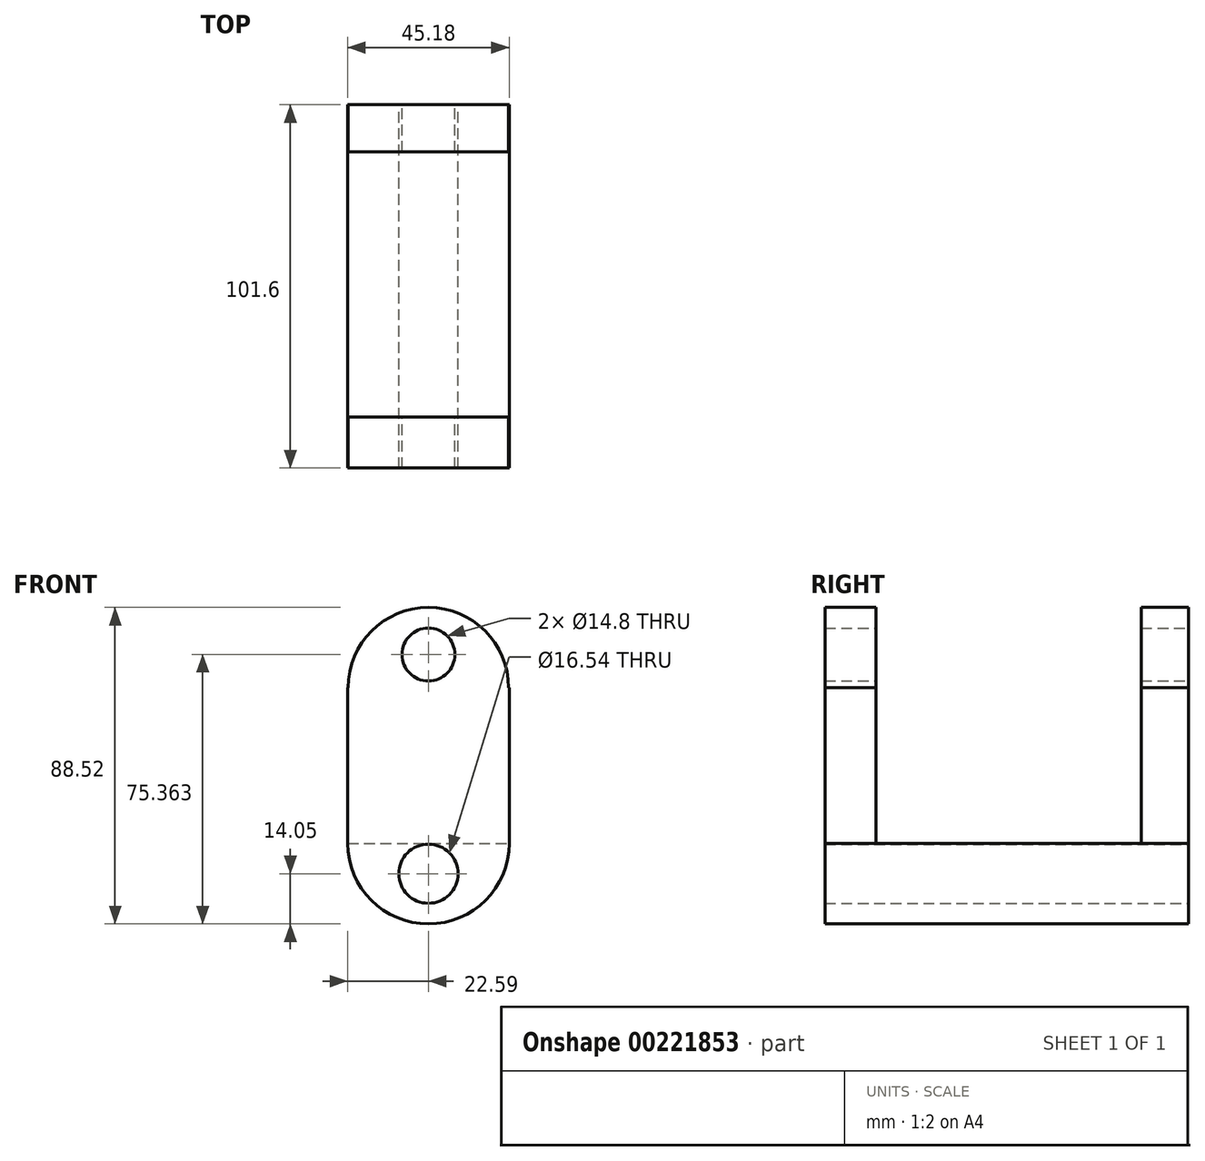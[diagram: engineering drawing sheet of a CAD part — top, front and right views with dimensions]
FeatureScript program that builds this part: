
annotation { "Feature Type Name" : "Feature", "Feature Type Description" : "" }
export const myFeature = defineFeature(function(context is Context, id is Id, definition is map)
    precondition{}
    {
        {
            var Q0;
            Q0=qCreatedBy(makeId("Front.planeOp"),FACE);
            var sketch = newSketch(context, id + "F0", { "sketchPlane" : qUnion([Q0])});
            skArc(sketch, "E0", {"start": v(-22.59, 0) * mm, "mid": v(0, -22.59) * mm, "end": v(22.59, 0) * mm});
            skLineSegment(sketch, "E1", {"start": v(0, 0) * mm, "end": v(0, -0.27) * mm});
            skCircle(sketch, "E2", {"center": v(0, -8.54) * mm, "radius": 8.27 * mm});
            skLineSegment(sketch, "E3.bottom", {"start": v(-22.6, 43.5) * mm, "end": v(-22.42, 43.5) * mm});
            skLineSegment(sketch, "E3.left", {"start": v(-22.6, 43.5) * mm, "end": v(-22.6, 0) * mm});
            skLineSegment(sketch, "E3.right", {"start": v(22.6, 43.5) * mm, "end": v(22.6, 0) * mm});
            skPoint(sketch, "E3.middle", {"position": v(0, -0.27) * mm});
            skLineSegment(sketch, "E4", {"start": v(-22.6, 0) * mm, "end": v(-22.59, 0) * mm});
            skLineSegment(sketch, "E5.trimOffspring", {"start": v(22.59, 0) * mm, "end": v(22.6, 0) * mm});
            skArc(sketch, "E6", {"start": v(22.42, 43.5) * mm, "mid": v(0, 65.93) * mm, "end": v(-22.42, 43.5) * mm});
            skLineSegment(sketch, "E7.trimOffspring", {"start": v(22.42, 43.5) * mm, "end": v(22.6, 43.5) * mm});
            skCircle(sketch, "E8", {"center": v(0, 52.77) * mm, "radius": 7.4 * mm});
            skSolve(sketch);
        }
        {
            var Q0;
            Q0 = qSketchRegion(id + "F0", true);
            extrude(context, id + "F1", {"entities" : qUnion([Q0]), "depth" : 50.8 * mm, "hasSecondDirection" : true, "secondDirectionOppositeDirection" : true, "secondDirectionDepth" : 50.8 * mm});
        }
        {
            var Q0;
            Q0=qCreatedBy(makeId("Right.planeOp"),FACE);
            var sketch = newSketch(context, id + "F2", { "sketchPlane" : qUnion([Q0])});
            skLineSegment(sketch, "E9.bottom", {"start": v(-36.51, 66.03) * mm, "end": v(37.62, 66.03) * mm});
            skLineSegment(sketch, "E9.top", {"start": v(-36.51, 0) * mm, "end": v(37.62, 0) * mm});
            skLineSegment(sketch, "E9.left", {"start": v(-36.51, 66.03) * mm, "end": v(-36.51, 0) * mm});
            skLineSegment(sketch, "E9.right", {"start": v(37.62, 66.03) * mm, "end": v(37.62, 0) * mm});
            skSolve(sketch);
        }
        {
            var Q0;
            Q0 = qSketchRegion(id + "F2", true);
            extrude(context, id + "F3", {"entities" : qUnion([Q0]), "operationType" : NewBodyOperationType.REMOVE, "oppositeDirection" : true, "depth" : 25.4 * mm, "hasSecondDirection" : true, "secondDirectionOppositeDirection" : false, "secondDirectionDepth" : 25.4 * mm});
        }
        {
            var Q0;
            Q0=qCreatedBy(makeId("Front.planeOp"),FACE);
            var sketch = newSketch(context, id + "F4", { "sketchPlane" : qUnion([Q0])});
            skArc(sketch, "E10", {"start": v(22.4, 0) * mm, "mid": v(-0.07, 18.06) * mm, "end": v(-22.53, 0) * mm});
            skSolve(sketch);
        }
        {
            var Q0;
            Q0=sQuery(id+"F4.wireOp",EDGE,"E10");
            extrude(context, id + "F5", {"bodyType" : ToolBodyType.SURFACE, "surfaceEntities" : qUnion([Q0]), "depth" : 36.83 * mm, "hasSecondDirection" : true, "secondDirectionOppositeDirection" : true, "secondDirectionDepth" : 37.34 * mm});
        }
    });
